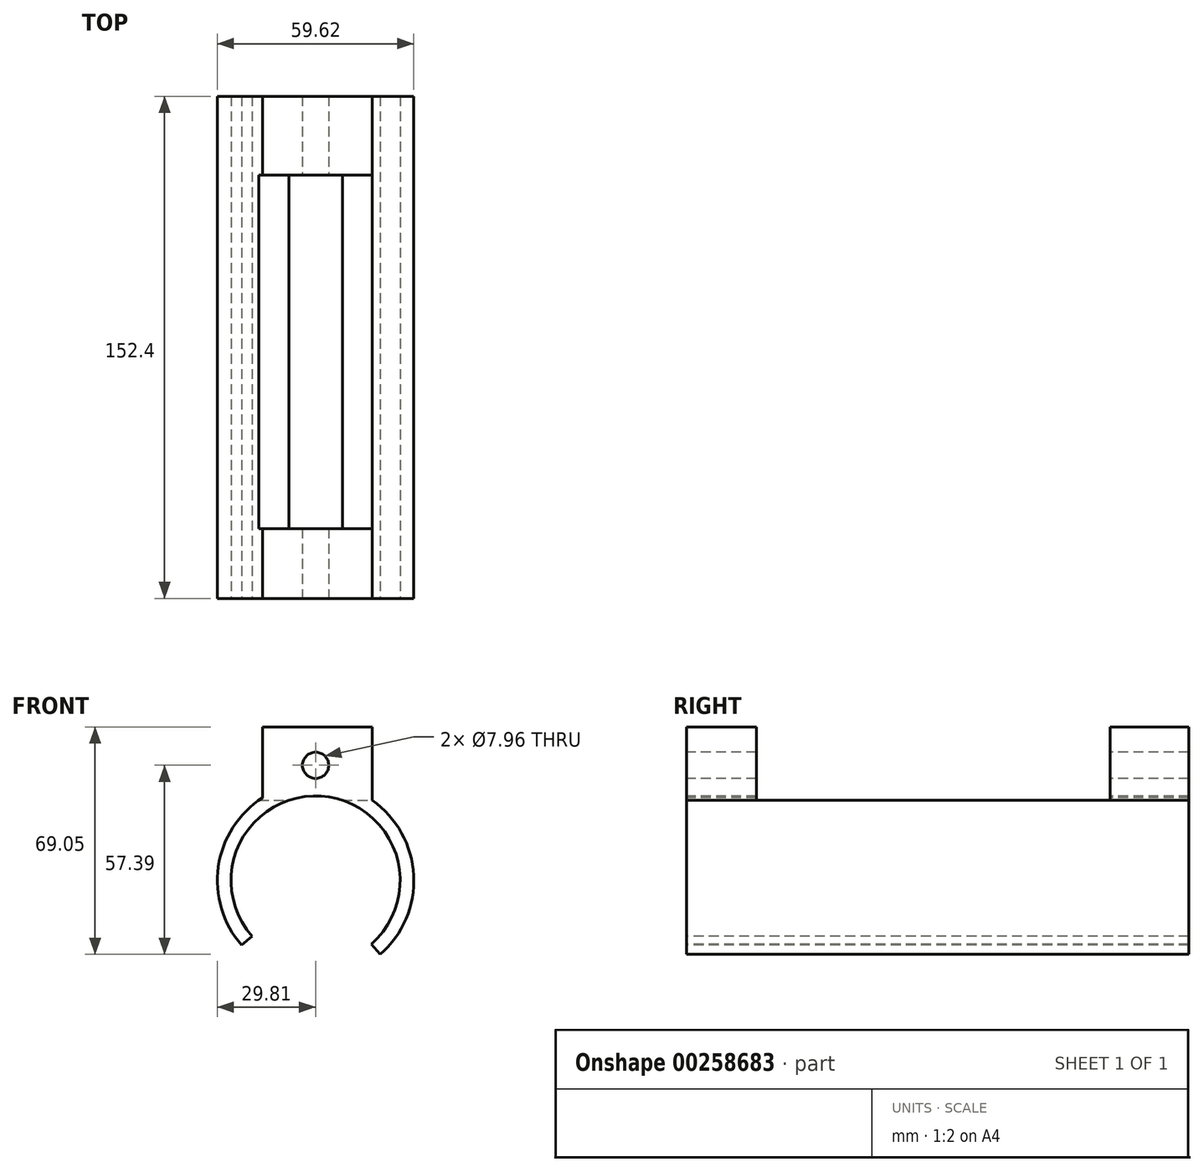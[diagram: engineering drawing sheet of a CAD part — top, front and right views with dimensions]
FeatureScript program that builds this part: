
annotation { "Feature Type Name" : "Feature", "Feature Type Description" : "" }
export const myFeature = defineFeature(function(context is Context, id is Id, definition is map)
    precondition{}
    {
        {
            var Q0;
            Q0=qCreatedBy(makeId("Front.planeOp"),FACE);
            var sketch = newSketch(context, id + "F0", { "sketchPlane" : qUnion([Q0])});
            skArc(sketch, "E0", {"start": v(16.9, -19.31) * mm, "mid": v(1.7, 25.6) * mm, "end": v(-19.31, -16.9) * mm});
            skArc(sketch, "E1", {"start": v(19.63, -22.43) * mm, "mid": v(29.77, 1.54) * mm, "end": v(17.22, 24.33) * mm});
            skLineSegment(sketch, "E2", {"start": v(-22.43, -19.63) * mm, "end": v(-19.31, -16.9) * mm});
            skLineSegment(sketch, "E3", {"start": v(16.9, -19.31) * mm, "end": v(19.63, -22.43) * mm});
            skLineSegment(sketch, "E4", {"start": v(-16.1, 25.09) * mm, "end": v(-16.1, 46.62) * mm});
            skLineSegment(sketch, "E5", {"start": v(-16.1, 46.62) * mm, "end": v(17.22, 46.62) * mm});
            skLineSegment(sketch, "E6", {"start": v(17.22, 46.62) * mm, "end": v(17.22, 24.33) * mm});
            skArc(sketch, "E7.trimOffspring", {"start": v(-16.1, 25.09) * mm, "mid": v(-29.51, 4.18) * mm, "end": v(-22.43, -19.63) * mm});
            skCircle(sketch, "E8", {"center": v(0, 34.96) * mm, "radius": 3.98 * mm});
            skSolve(sketch);
        }
        {
            var Q0;
            Q0=makeQuery(id+"F0.imprint","IMPRINT",FACE,{"disambiguationData":[TD([[makeQuery(id+"F0.imprint","IMPRINT",EDGE,{"derivedFrom":sQuery(id+"F0.wireOp",EDGE,"E0")}),-1.0]])]});
            extrude(context, id + "F1", {"entities" : qUnion([Q0]), "oppositeDirection" : true, "depth" : 152.4 * mm});
        }
        {
            var Q0;
            Q0=makeQuery(id+"F1.opExtrude","SWEPT_FACE",FACE,{"disambiguationData":[OSD([sQuery(id+"F0.wireOp",EDGE,"E6")])]});
            var sketch = newSketch(context, id + "F2", { "sketchPlane" : qUnion([Q0])});
            skLineSegment(sketch, "E9", {"start": v(21.2, 46.62) * mm, "end": v(21.2, 24.33) * mm});
            skLineSegment(sketch, "E10", {"start": v(128.53, 46.62) * mm, "end": v(128.53, 24.33) * mm});
            skSolve(sketch);
        }
        {
            var Q0;
            Q0 = qSketchRegion(id + "F2", true);
            var Q1;
            {var subQ0=sQuery(id+"F2.wireOp",EDGE,"E9");Q1=makeQuery(id+"F2.imprint","IMPRINT",FACE,{"disambiguationData":[TD([[makeQuery(id+"F2.imprint","IMPRINT",EDGE,{"derivedFrom":subQ0}),1.0]])]});}
            extrude(context, id + "F3", {"entities" : qUnion([Q0, Q1]), "operationType" : NewBodyOperationType.REMOVE, "endBound" : BoundingType.THROUGH_ALL, "oppositeDirection" : true, "depth" : 25.4 * mm});
        }
    });
